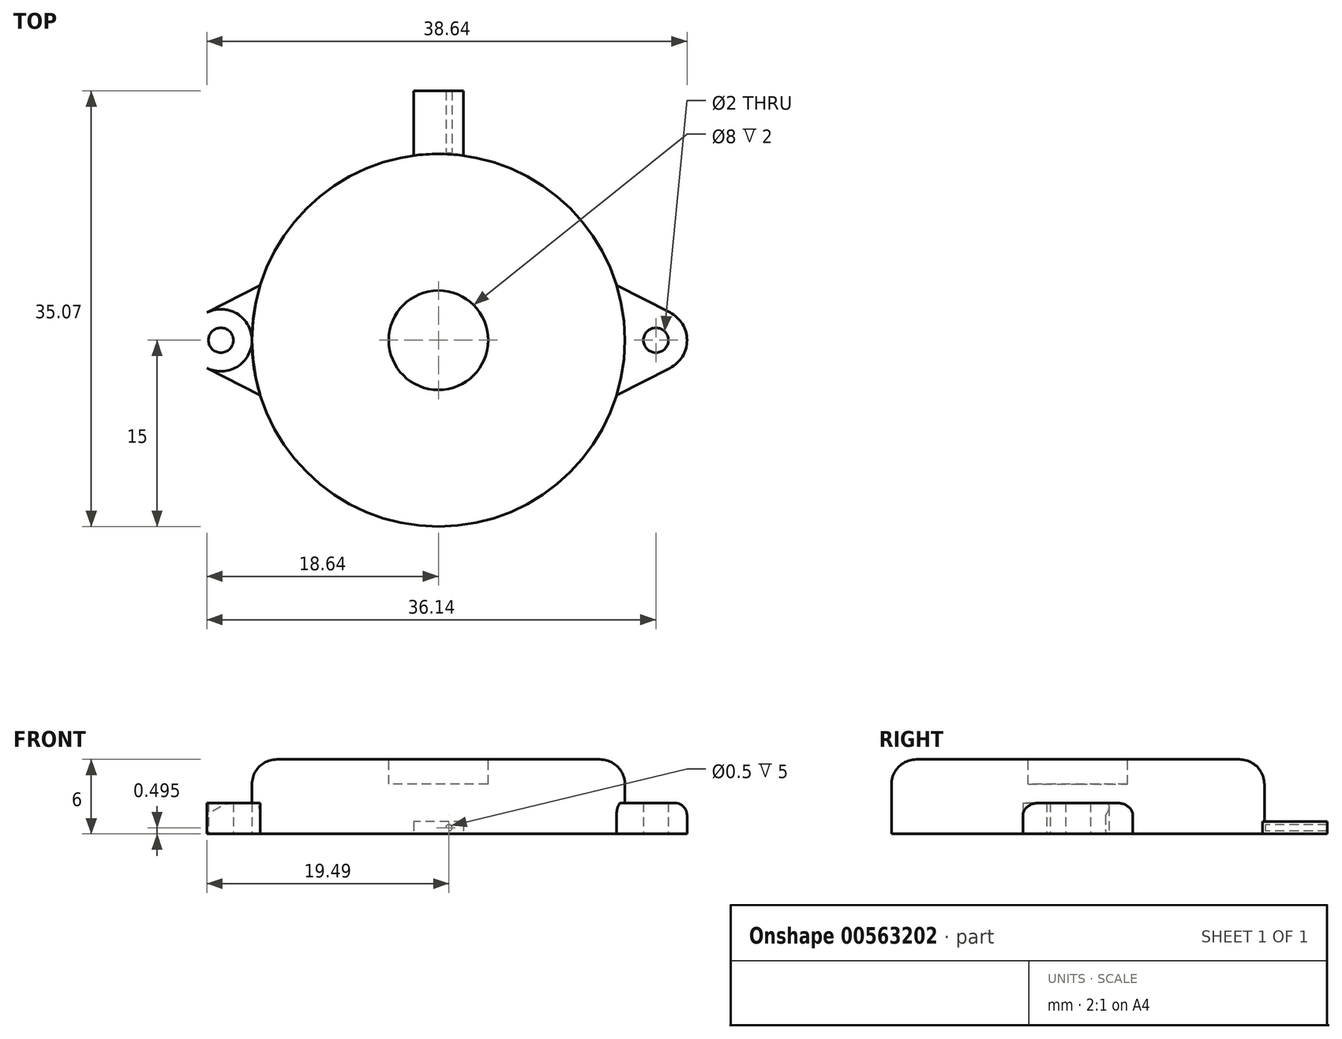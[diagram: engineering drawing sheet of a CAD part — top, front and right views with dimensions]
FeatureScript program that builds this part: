
annotation { "Feature Type Name" : "Feature", "Feature Type Description" : "" }
export const myFeature = defineFeature(function(context is Context, id is Id, definition is map)
    precondition{}
    {
        {
            var Q0;
            Q0=qCreatedBy(makeId("Top.planeOp"),FACE);
            var sketch = newSketch(context, id + "F0", { "sketchPlane" : qUnion([Q0])});
            skCircle(sketch, "E0", {"center": v(0, 0) * mm, "radius": 15 * mm});
            skLineSegment(sketch, "E1", {"start": v(0, 0) * mm, "end": v(48.93, 0) * mm, "construction": true});
            skLineSegment(sketch, "E2", {"start": v(0, 0) * mm, "end": v(0, 21.8) * mm, "construction": true});
            skCircle(sketch, "E3", {"center": v(17.5, 0) * mm, "radius": 1 * mm});
            skCircle(sketch, "E4", {"center": v(17.5, 0) * mm, "radius": 2.5 * mm});
            skLineSegment(sketch, "E5", {"start": v(14.33, 4.42) * mm, "end": v(18.64, 2.23) * mm});
            skLineSegment(sketch, "E6.MirrorCS", {"start": v(14.33, -4.42) * mm, "end": v(18.64, -2.23) * mm});
            skLineSegment(sketch, "E7.MirrorCS", {"start": v(-14.33, 4.42) * mm, "end": v(-18.64, 2.23) * mm});
            skCircle(sketch, "E8.MirrorC", {"center": v(-17.5, 0) * mm, "radius": 2.5 * mm});
            skLineSegment(sketch, "E9.MirrorCS", {"start": v(-14.33, -4.42) * mm, "end": v(-18.64, -2.23) * mm});
            skCircle(sketch, "E10.MirrorC", {"center": v(-17.5, 0) * mm, "radius": 1 * mm});
            skLineSegment(sketch, "E11", {"start": v(-2, 14.87) * mm, "end": v(-2, 15.07) * mm});
            skLineSegment(sketch, "E12", {"start": v(-2, 15.07) * mm, "end": v(0, 15.07) * mm});
            skLineSegment(sketch, "E13.MirrorCS", {"start": v(2, 15.07) * mm, "end": v(0, 15.07) * mm});
            skLineSegment(sketch, "E14.MirrorCS", {"start": v(2, 14.87) * mm, "end": v(2, 15.07) * mm});
            skSolve(sketch);
        }
        {
            var Q0;
            {var subQ0=sQuery(id+"F0.wireOp",EDGE,"E0");var subQ1=makeQuery(id+"F0.imprint","INTERSECT",VERTEX,{"derivedFrom":[subQ0,sQuery(id+"F0.wireOp",EDGE,"E5")]});Q0=makeQuery(id+"F0.imprint","IMPRINT",FACE,{"disambiguationData":[TD([[makeQuery(id+"F0.imprint","IMPRINT",EDGE,{"disambiguationData":[TD([[subQ1,-1.0]])],"derivedFrom":subQ0}),1.0]])]});}
            extrude(context, id + "F1", {"entities" : qUnion([Q0]), "depth" : 6 * mm, "offsetDistance" : 25 * mm});
        }
        {
            var Q0;
            {var subQ0=sQuery(id+"F0.wireOp",EDGE,"E7.MirrorCS");Q0=makeQuery(id+"F0.imprint","IMPRINT",FACE,{"disambiguationData":[TD([[makeQuery(id+"F0.imprint","IMPRINT",EDGE,{"derivedFrom":subQ0}),1.0]])]});}
            var Q1;
            Q1=makeQuery(id+"F0.imprint","IMPRINT",FACE,{"disambiguationData":[TD([[makeQuery(id+"F0.imprint","IMPRINT",EDGE,{"derivedFrom":sQuery(id+"F0.wireOp",EDGE,"E10.MirrorC")}),1.0]])]});
            var Q2;
            {var subQ0=sQuery(id+"F0.wireOp",EDGE,"E5");Q2=makeQuery(id+"F0.imprint","IMPRINT",FACE,{"disambiguationData":[TD([[makeQuery(id+"F0.imprint","IMPRINT",EDGE,{"derivedFrom":subQ0}),-1.0]])]});}
            var Q3;
            Q3=makeQuery(id+"F0.imprint","IMPRINT",FACE,{"disambiguationData":[TD([[makeQuery(id+"F0.imprint","IMPRINT",EDGE,{"derivedFrom":sQuery(id+"F0.wireOp",EDGE,"E3")}),-1.0]])]});
            var Q4;
            {var subQ0=sQuery(id+"F0.wireOp",EDGE,"E6.MirrorCS");Q4=makeQuery(id+"F0.imprint","IMPRINT",FACE,{"disambiguationData":[TD([[makeQuery(id+"F0.imprint","IMPRINT",EDGE,{"derivedFrom":subQ0}),1.0]])]});}
            var Q5;
            {var subQ0=sQuery(id+"F0.wireOp",EDGE,"E9.MirrorCS");Q5=makeQuery(id+"F0.imprint","IMPRINT",FACE,{"disambiguationData":[TD([[makeQuery(id+"F0.imprint","IMPRINT",EDGE,{"derivedFrom":subQ0}),-1.0]])]});}
            extrude(context, id + "F2", {"entities" : qUnion([Q0, Q1, Q2, Q3, Q4, Q5]), "operationType" : NewBodyOperationType.ADD, "depth" : 2.5 * mm, "offsetDistance" : 25 * mm});
        }
        {
            var Q0;
            Q0=makeQuery(id+"F1.opExtrude","CAP_FACE",FACE,{"disambiguationData":[OSD([sQuery(id+"F0.wireOp",EDGE,"E0")])],"isStart":false});
            var sketch = newSketch(context, id + "F3", { "sketchPlane" : qUnion([Q0])});
            skCircle(sketch, "E15", {"center": v(0, 0) * mm, "radius": 4 * mm});
            skSolve(sketch);
        }
        {
            var Q0;
            Q0=makeQuery(id+"F3.imprint","IMPRINT",FACE,{"disambiguationData":[TD([[makeQuery(id+"F3.imprint","IMPRINT",EDGE,{"derivedFrom":sQuery(id+"F3.wireOp",EDGE,"E15")}),1.0]])]});
            extrude(context, id + "F4", {"entities" : qUnion([Q0]), "operationType" : NewBodyOperationType.REMOVE, "oppositeDirection" : true, "depth" : 2 * mm, "offsetDistance" : 25 * mm});
        }
        {
            var Q0;
            Q0=makeQuery(id+"F1.opExtrude","CAP_EDGE",EDGE,{"disambiguationData":[OSD([sQuery(id+"F0.wireOp",EDGE,"E0")])],"isStart":false});
            fillet(context, id + "F5", {"entities" : qUnion([Q0]), "radius" : 2 * mm, "tangentPropagation" : true, "allowEdgeOverflow" : false});
        }
        {
            var Q0;
            {var subQ0=sQuery(id+"F0.wireOp",EDGE,"E11");Q0=makeQuery(id+"F0.imprint","IMPRINT",FACE,{"disambiguationData":[TD([[makeQuery(id+"F0.imprint","IMPRINT",EDGE,{"derivedFrom":subQ0}),-1.0]])]});}
            extrude(context, id + "F6", {"entities" : qUnion([Q0]), "operationType" : NewBodyOperationType.ADD, "depth" : 1 * mm, "offsetDistance" : 25 * mm});
        }
        {
            var Q0;
            Q0=makeQuery(id+"F6.opExtrude","SWEPT_FACE",FACE,{"disambiguationData":[OSD([sQuery(id+"F0.wireOp",EDGE,"E12"),sQuery(id+"F0.wireOp",EDGE,"E13.MirrorCS")])]});
            var sketch = newSketch(context, id + "F7", { "sketchPlane" : qUnion([Q0])});
            skCircle(sketch, "E16", {"center": v(0.85, 0.5) * mm, "radius": 0.25 * mm});
            skCircle(sketch, "E17.MirrorC", {"center": v(-0.85, 0.5) * mm, "radius": 0.25 * mm});
            skSolve(sketch);
        }
        {
            var Q0;
            Q0=makeQuery(id+"F7.imprint","IMPRINT",FACE,{"disambiguationData":[TD([[makeQuery(id+"F7.imprint","IMPRINT",EDGE,{"derivedFrom":sQuery(id+"F7.wireOp",EDGE,"E17.MirrorC")}),-1.0]])]});
            var Q1;
            Q1=makeQuery(id+"F7.imprint","IMPRINT",FACE,{"disambiguationData":[TD([[makeQuery(id+"F7.imprint","IMPRINT",EDGE,{"derivedFrom":sQuery(id+"F7.wireOp",EDGE,"E16")}),1.0]])]});
            extrude(context, id + "F8", {"entities" : qUnion([Q0, Q1]), "operationType" : NewBodyOperationType.ADD, "depth" : 5 * mm, "offsetDistance" : 25 * mm});
        }
        {
            var Q0;
            Q0=makeQuery(id+"F2.opExtrude","CAP_EDGE",EDGE,{"disambiguationData":[OSD([sQuery(id+"F0.wireOp",EDGE,"E6.MirrorCS")])],"isStart":false});
            var Q1;
            Q1=makeQuery(id+"F2.opExtrude","CAP_EDGE",EDGE,{"disambiguationData":[OSD([sQuery(id+"F0.wireOp",EDGE,"E7.MirrorCS")])],"isStart":false});
            var Q2;
            Q2=makeQuery(id+"F4.boolean.opBoolean","COPY",EDGE,{"derivedFrom":makeQuery(id+"F4.opExtrude","CAP_EDGE",EDGE,{"disambiguationData":[OSD([sQuery(id+"F3.wireOp",EDGE,"E15")])],"isStart":true})});
            fillet(context, id + "F9", {"entities" : qUnion([Q0, Q1, Q2]), "radius" : 1 * mm, "tangentPropagation" : true, "allowEdgeOverflow" : false});
        }
    });
